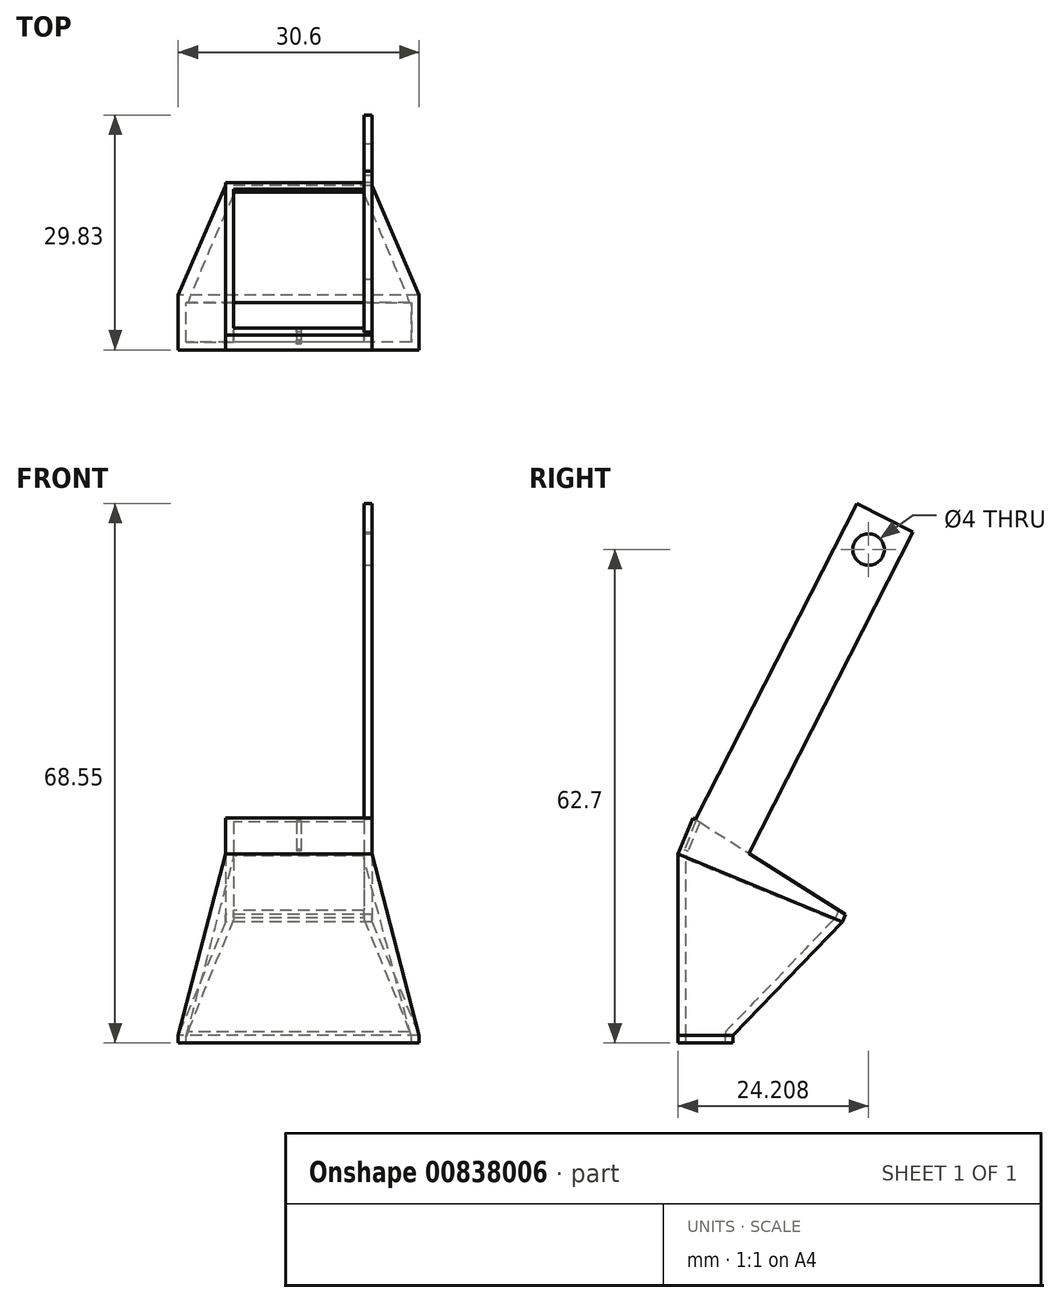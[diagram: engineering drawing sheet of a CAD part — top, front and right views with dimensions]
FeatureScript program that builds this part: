
annotation { "Feature Type Name" : "Feature", "Feature Type Description" : "" }
export const myFeature = defineFeature(function(context is Context, id is Id, definition is map)
    precondition{}
    {
        {
            var Q0;
            Q0=qCreatedBy(makeId("Right.planeOp"),FACE);
            var sketch = newSketch(context, id + "F0", { "sketchPlane" : qUnion([Q0])});
            skLineSegment(sketch, "E0", {"start": v(0, 0) * mm, "end": v(20.9, -8.6) * mm});
            skLineSegment(sketch, "E1", {"start": v(20.9, -8.6) * mm, "end": v(21.28, -7.68) * mm});
            skLineSegment(sketch, "E2", {"start": v(21.28, -7.68) * mm, "end": v(0.38, 0.92) * mm});
            skLineSegment(sketch, "E3", {"start": v(0.38, 0.92) * mm, "end": v(0, 0) * mm});
            skLineSegment(sketch, "E4", {"start": v(0.38, 0.92) * mm, "end": v(1.9, 4.62) * mm});
            skLineSegment(sketch, "E5", {"start": v(1.9, 4.62) * mm, "end": v(21.28, -7.68) * mm});
            skSolve(sketch);
        }
        {
            var Q0;
            Q0 = qSketchRegion(id + "F0", true);
            extrude(context, id + "F1", {"entities" : qUnion([Q0]), "depth" : 18.6 * mm, "offsetDistance" : 25 * mm});
        }
        {
            var Q0;
            Q0=qCreatedBy(makeId("Top.planeOp"),FACE);
            cPlane(context, id + "F2", {"entities" : qUnion([Q0]), "cplaneType" : CPlaneType.OFFSET, "offset" : 23 * mm, "oppositeDirection" : true, "width" : 150 * mm, "height" : 150 * mm});
        }
        {
            var Q0;
            Q0=qCreatedBy(id+"F2.planeOp",FACE);
            var sketch = newSketch(context, id + "F3", { "sketchPlane" : qUnion([Q0])});
            skLineSegment(sketch, "E6.bottom", {"start": v(24.6, 7) * mm, "end": v(-6, 7) * mm});
            skLineSegment(sketch, "E6.top", {"start": v(-6, 0) * mm, "end": v(24.6, 0) * mm});
            skLineSegment(sketch, "E6.left", {"start": v(-6, 7) * mm, "end": v(-6, 0) * mm});
            skLineSegment(sketch, "E6.right", {"start": v(24.6, 7) * mm, "end": v(24.6, 0) * mm});
            skSolve(sketch);
        }
        {
            var Q1;
            Q1=makeQuery(id+"F1.opExtrude","SWEPT_FACE",FACE,{"disambiguationData":[OSD([sQuery(id+"F0.wireOp",EDGE,"E0")])]});
            var Q2;
            Q2 = qSketchRegion(id + "F3", true);
            loft(context, id + "F4", {"operationType" : NewBodyOperationType.ADD, "sheetProfilesArray" : [{ "sheetProfileEntities" : qUnion([Q1]) }, { "sheetProfileEntities" : qUnion([Q2]) }]});
        }
        {
            var Q0;
            Q0 = qSketchRegion(id + "F3", true);
            extrude(context, id + "F5", {"entities" : qUnion([Q0]), "operationType" : NewBodyOperationType.ADD, "oppositeDirection" : true, "depth" : 5 * mm, "offsetDistance" : 25 * mm});
        }
        {
            var Q0;
            Q0=makeQuery(id+"F1.opExtrude","SWEPT_FACE",FACE,{"disambiguationData":[OSD([sQuery(id+"F0.wireOp",EDGE,"E5")])]});
            shell(context, id + "F6", {"entities" : qUnion([Q0]), "thickness" : 1 * mm});
        }
        {
            var Q0;
            Q0=makeQuery(id+"F5.opExtrude","CAP_FACE",FACE,{"disambiguationData":[OSD([sQuery(id+"F3.wireOp",EDGE,"E6.bottom"),sQuery(id+"F3.wireOp",EDGE,"E6.top"),sQuery(id+"F3.wireOp",EDGE,"E6.left"),sQuery(id+"F3.wireOp",EDGE,"E6.right")])],"isStart":false});
            extrude(context, id + "F7", {"entities" : qUnion([Q0]), "operationType" : NewBodyOperationType.REMOVE, "oppositeDirection" : true, "depth" : 4 * mm, "offsetDistance" : 25 * mm});
        }
        {
            var Q0;
            Q0=makeQuery(id+"F1.opExtrude","CAP_FACE",FACE,{"disambiguationData":[OSD([sQuery(id+"F0.wireOp",EDGE,"E0"),sQuery(id+"F0.wireOp",EDGE,"E1"),sQuery(id+"F0.wireOp",EDGE,"E2"),sQuery(id+"F0.wireOp",EDGE,"E3")])],"isStart":false});
            var sketch = newSketch(context, id + "F8", { "sketchPlane" : qUnion([Q0])});
            skLineSegment(sketch, "E7", {"start": v(0, 0) * mm, "end": v(22.7, 44.55) * mm});
            skLineSegment(sketch, "E8", {"start": v(22.7, 44.55) * mm, "end": v(29.83, 40.92) * mm});
            skLineSegment(sketch, "E9", {"start": v(29.83, 40.92) * mm, "end": v(7.42, -3.05) * mm});
            skPoint(sketch, "E10", {"position": v(24.2, 38.7) * mm});
            skLineSegment(sketch, "E11", {"start": v(7.42, -3.05) * mm, "end": v(0, 0) * mm});
            skCircle(sketch, "E12", {"center": v(24.2, 38.7) * mm, "radius": 2 * mm});
            skSolve(sketch);
        }
        {
            var Q0;
            Q0 = qSketchRegion(id + "F8", true);
            extrude(context, id + "F9", {"entities" : qUnion([Q0]), "operationType" : NewBodyOperationType.ADD, "oppositeDirection" : true, "depth" : 1 * mm, "offsetDistance" : 25 * mm});
        }
        {
            var Q0;
            Q0=makeQuery(id+"F6.opShell","OFFSET_FACE",FACE,{"disambiguationData":[OSD([sQuery(id+"F0.wireOp",EDGE,"E3"),sQuery(id+"F0.wireOp",EDGE,"E4")])]});
            var sketch = newSketch(context, id + "F10", { "sketchPlane" : qUnion([Q0])});
            skLineSegment(sketch, "E13.bottom", {"start": v(-9.6, 4.82) * mm, "end": v(-9, 4.82) * mm});
            skLineSegment(sketch, "E13.top", {"start": v(-9.6, 0.82) * mm, "end": v(-9, 0.82) * mm});
            skLineSegment(sketch, "E13.left", {"start": v(-9.6, 4.82) * mm, "end": v(-9.6, 0.82) * mm});
            skLineSegment(sketch, "E13.right", {"start": v(-9, 4.82) * mm, "end": v(-9, 0.82) * mm});
            skSolve(sketch);
        }
        {
            var Q0;
            Q0=makeQuery(id+"F10.imprint","IMPRINT",FACE,{"disambiguationData":[TD([[makeQuery(id+"F10.imprint","IMPRINT",EDGE,{"derivedFrom":sQuery(id+"F10.wireOp",EDGE,"E13.bottom")}),-1.0]])]});
            extrude(context, id + "F11", {"entities" : qUnion([Q0]), "operationType" : NewBodyOperationType.REMOVE, "oppositeDirection" : true, "depth" : 0.5 * mm, "offsetDistance" : 25 * mm});
        }
    });
